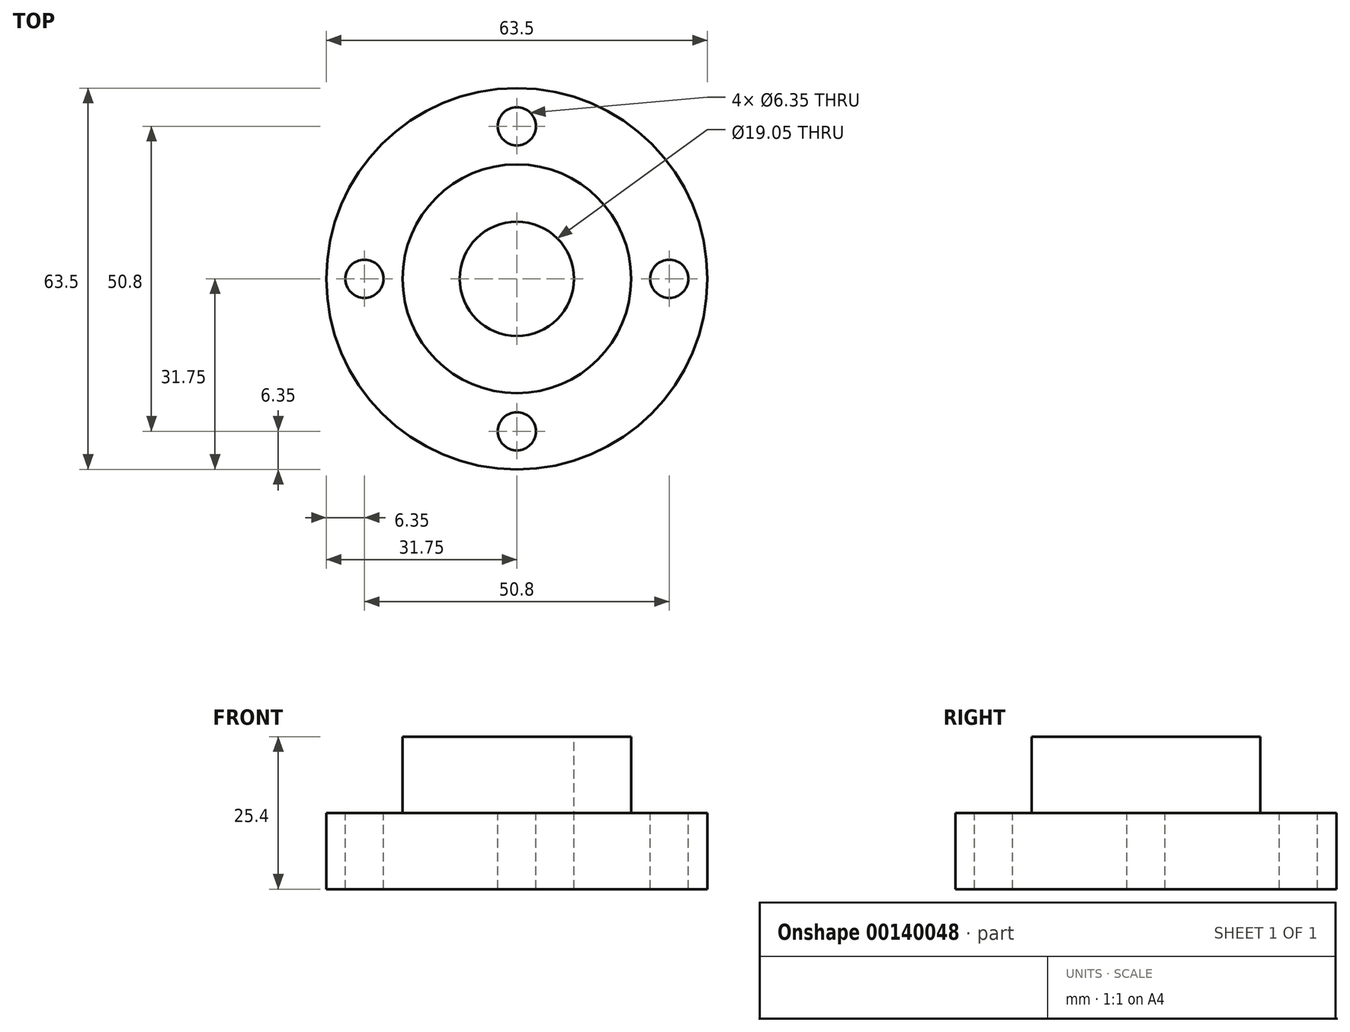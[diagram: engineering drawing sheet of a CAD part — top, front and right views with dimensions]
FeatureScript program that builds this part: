
annotation { "Feature Type Name" : "Feature", "Feature Type Description" : "" }
export const myFeature = defineFeature(function(context is Context, id is Id, definition is map)
    precondition{}
    {
        {
            var Q0;
            Q0=qCreatedBy(makeId("Top.planeOp"),FACE);
            var sketch = newSketch(context, id + "F0", { "sketchPlane" : qUnion([Q0])});
            skCircle(sketch, "E0", {"center": v(0, 0) * mm, "radius": 31.75 * mm});
            skCircle(sketch, "E1", {"center": v(0, 0) * mm, "radius": 19.05 * mm});
            skSolve(sketch);
        }
        {
            var Q0;
            Q0=makeQuery(id+"F0.imprint","IMPRINT",FACE,{"disambiguationData":[TD([[makeQuery(id+"F0.imprint","IMPRINT",EDGE,{"derivedFrom":sQuery(id+"F0.wireOp",EDGE,"E1")}),1.0]])]});
            var Q1;
            Q1=makeQuery(id+"F0.imprint","IMPRINT",FACE,{"disambiguationData":[TD([[makeQuery(id+"F0.imprint","IMPRINT",EDGE,{"derivedFrom":sQuery(id+"F0.wireOp",EDGE,"E0")}),1.0]])]});
            extrude(context, id + "F1", {"entities" : qUnion([Q0, Q1]), "depth" : 12.7 * mm});
        }
        {
            var Q0;
            Q0=makeQuery(id+"F0.imprint","IMPRINT",FACE,{"disambiguationData":[TD([[makeQuery(id+"F0.imprint","IMPRINT",EDGE,{"derivedFrom":sQuery(id+"F0.wireOp",EDGE,"E1")}),1.0]])]});
            extrude(context, id + "F2", {"entities" : qUnion([Q0]), "operationType" : NewBodyOperationType.ADD, "depth" : 25.4 * mm});
        }
        {
            var Q0;
            Q0=makeQuery(id+"F2.opExtrude","CAP_FACE",FACE,{"disambiguationData":[OSD([sQuery(id+"F0.wireOp",EDGE,"E1")])],"isStart":false});
            var sketch = newSketch(context, id + "F3", { "sketchPlane" : qUnion([Q0])});
            skCircle(sketch, "E2", {"center": v(0, 0) * mm, "radius": 9.53 * mm});
            skSolve(sketch);
        }
        {
            var Q0;
            Q0=makeQuery(id+"F3.imprint","IMPRINT",FACE,{"disambiguationData":[TD([[makeQuery(id+"F3.imprint","IMPRINT",EDGE,{"derivedFrom":sQuery(id+"F3.wireOp",EDGE,"E2")}),1.0]])]});
            extrude(context, id + "F4", {"entities" : qUnion([Q0]), "operationType" : NewBodyOperationType.REMOVE, "endBound" : BoundingType.THROUGH_ALL, "oppositeDirection" : true, "depth" : 25.4 * mm});
        }
        {
            var Q0;
            Q0=makeQuery(id+"F1.opExtrude","CAP_FACE",FACE,{"disambiguationData":[OSD([sQuery(id+"F0.wireOp",EDGE,"E0")])],"isStart":false});
            var sketch = newSketch(context, id + "F5", { "sketchPlane" : qUnion([Q0])});
            skCircle(sketch, "E3", {"center": v(0, 0) * mm, "radius": 25.4 * mm, "construction": true});
            skCircle(sketch, "E4", {"center": v(0, 25.4) * mm, "radius": 3.18 * mm});
            skCircle(sketch, "E5.1.0", {"center": v(-25.4, 0) * mm, "radius": 3.18 * mm});
            skCircle(sketch, "E5.2.0", {"center": v(0, -25.4) * mm, "radius": 3.18 * mm});
            skCircle(sketch, "E5.3.0", {"center": v(25.4, 0) * mm, "radius": 3.18 * mm});
            skSolve(sketch);
        }
        {
            var Q0;
            Q0=makeQuery(id+"F5.imprint","IMPRINT",FACE,{"disambiguationData":[TD([[makeQuery(id+"F5.imprint","IMPRINT",EDGE,{"derivedFrom":sQuery(id+"F5.wireOp",EDGE,"E5.1.0")}),1.0]])]});
            var Q1;
            Q1=makeQuery(id+"F5.imprint","IMPRINT",FACE,{"disambiguationData":[TD([[makeQuery(id+"F5.imprint","IMPRINT",EDGE,{"derivedFrom":sQuery(id+"F5.wireOp",EDGE,"E5.2.0")}),1.0]])]});
            var Q2;
            Q2=makeQuery(id+"F5.imprint","IMPRINT",FACE,{"disambiguationData":[TD([[makeQuery(id+"F5.imprint","IMPRINT",EDGE,{"derivedFrom":sQuery(id+"F5.wireOp",EDGE,"E5.3.0")}),1.0]])]});
            var Q3;
            Q3=makeQuery(id+"F5.imprint","IMPRINT",FACE,{"disambiguationData":[TD([[makeQuery(id+"F5.imprint","IMPRINT",EDGE,{"derivedFrom":sQuery(id+"F5.wireOp",EDGE,"E4")}),1.0]])]});
            extrude(context, id + "F6", {"entities" : qUnion([Q0, Q1, Q2, Q3]), "operationType" : NewBodyOperationType.REMOVE, "endBound" : BoundingType.THROUGH_ALL, "oppositeDirection" : true, "depth" : 25.4 * mm});
        }
    });
